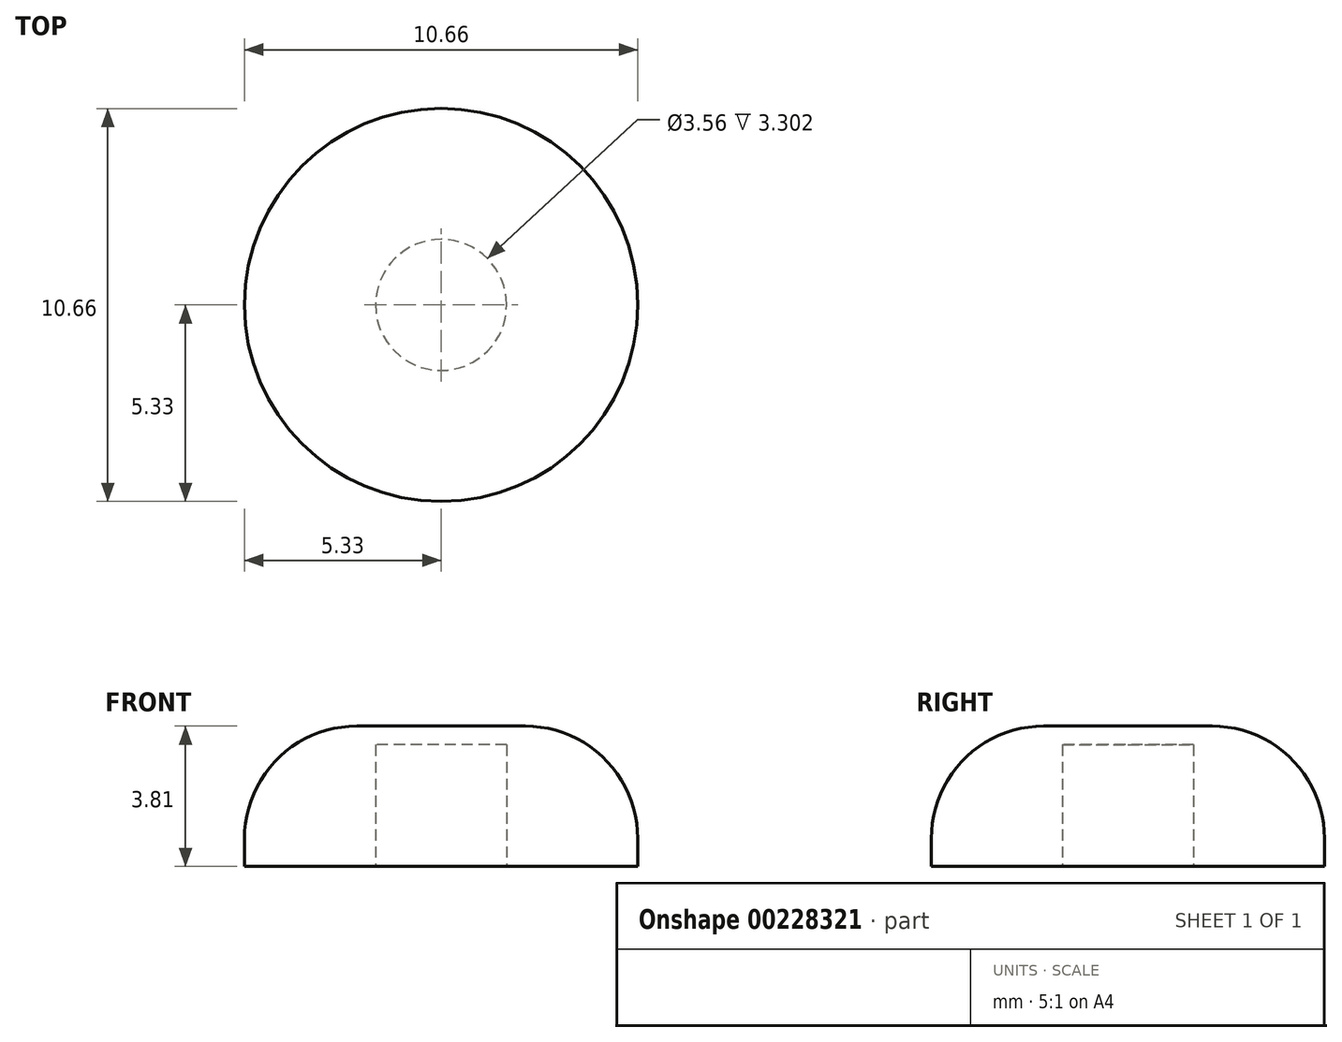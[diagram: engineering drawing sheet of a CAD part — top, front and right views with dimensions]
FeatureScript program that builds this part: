
annotation { "Feature Type Name" : "Feature", "Feature Type Description" : "" }
export const myFeature = defineFeature(function(context is Context, id is Id, definition is map)
    precondition{}
    {
        {
            var Q0;
            Q0=qCreatedBy(makeId("Top.planeOp"),FACE);
            var sketch = newSketch(context, id + "F0", { "sketchPlane" : qUnion([Q0])});
            skCircle(sketch, "E0", {"center": v(0, 0) * mm, "radius": 5.33 * mm});
            skCircle(sketch, "E1", {"center": v(0, 0) * mm, "radius": 1.78 * mm});
            skSolve(sketch);
        }
        {
            var Q0;
            Q0=makeQuery(id+"F0.imprint","IMPRINT",FACE,{"disambiguationData":[TD([[makeQuery(id+"F0.imprint","IMPRINT",EDGE,{"derivedFrom":sQuery(id+"F0.wireOp",EDGE,"E0")}),1.0]])]});
            var Q1;
            Q1=makeQuery(id+"F0.imprint","IMPRINT",FACE,{"disambiguationData":[TD([[makeQuery(id+"F0.imprint","IMPRINT",EDGE,{"derivedFrom":sQuery(id+"F0.wireOp",EDGE,"E1")}),1.0]])]});
            extrude(context, id + "F1", {"entities" : qUnion([Q0, Q1]), "depth" : 3.8 * mm});
        }
        {
            var Q0;
            Q0=makeQuery(id+"F1.opExtrude","CAP_EDGE",EDGE,{"disambiguationData":[OSD([sQuery(id+"F0.wireOp",EDGE,"E0")])],"isStart":false});
            fillet(context, id + "F2", {"entities" : qUnion([Q0]), "radius" : 3.05 * mm, "tangentPropagation" : true, "allowEdgeOverflow" : false});
        }
        {
            var Q0;
            Q0=makeQuery(id+"F0.imprint","IMPRINT",FACE,{"disambiguationData":[TD([[makeQuery(id+"F0.imprint","IMPRINT",EDGE,{"derivedFrom":sQuery(id+"F0.wireOp",EDGE,"E1")}),1.0]])]});
            extrude(context, id + "F3", {"entities" : qUnion([Q0]), "operationType" : NewBodyOperationType.REMOVE, "depth" : 3.3 * mm});
        }
    });
